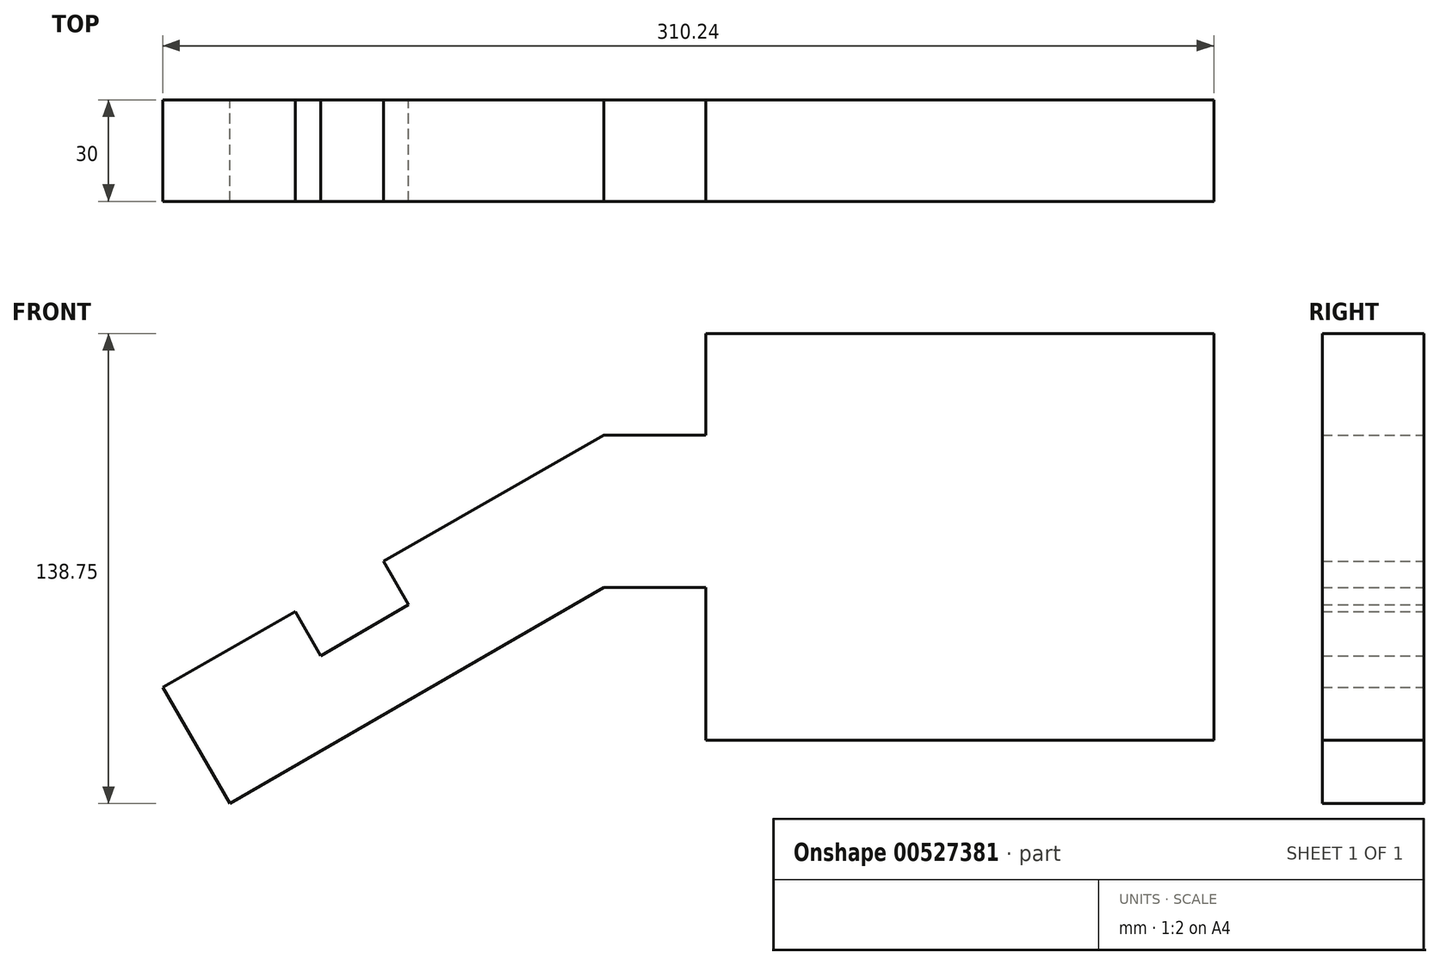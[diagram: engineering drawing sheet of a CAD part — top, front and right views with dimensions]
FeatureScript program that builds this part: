
annotation { "Feature Type Name" : "Feature", "Feature Type Description" : "" }
export const myFeature = defineFeature(function(context is Context, id is Id, definition is map)
    precondition{}
    {
        {
            var Q0;
            Q0=qCreatedBy(makeId("Front.planeOp"),FACE);
            var sketch = newSketch(context, id + "F0", { "sketchPlane" : qUnion([Q0])});
            skLineSegment(sketch, "E0", {"start": v(0, 0) * mm, "end": v(150, 0) * mm});
            skLineSegment(sketch, "E1", {"start": v(150, 0) * mm, "end": v(150, 120) * mm});
            skLineSegment(sketch, "E2", {"start": v(150, 120) * mm, "end": v(0, 120) * mm});
            skLineSegment(sketch, "E3", {"start": v(0, 0) * mm, "end": v(0, 45) * mm});
            skLineSegment(sketch, "E4", {"start": v(0, 120) * mm, "end": v(0, 90) * mm});
            skLineSegment(sketch, "E5", {"start": v(0, 90) * mm, "end": v(-30, 90) * mm});
            skLineSegment(sketch, "E6", {"start": v(0, 45) * mm, "end": v(-30, 45) * mm});
            skLineSegment(sketch, "E7", {"start": v(0, 90) * mm, "end": v(90, 90) * mm});
            skLineSegment(sketch, "E8", {"start": v(0, 45) * mm, "end": v(90, 45) * mm});
            skLineSegment(sketch, "E9", {"start": v(90, 45) * mm, "end": v(90, 90) * mm});
            skLineSegment(sketch, "E10", {"start": v(-30, 45) * mm, "end": v(-140.42, -18.75) * mm});
            skLineSegment(sketch, "E11", {"start": v(-140.42, -18.75) * mm, "end": v(-160.24, 15.58) * mm});
            skLineSegment(sketch, "E12", {"start": v(-30, 90) * mm, "end": v(-95.12, 52.8) * mm});
            skLineSegment(sketch, "E13", {"start": v(-121.1, 37.95) * mm, "end": v(-113.66, 24.92) * mm});
            skLineSegment(sketch, "E14", {"start": v(-113.66, 24.92) * mm, "end": v(-87.68, 39.92) * mm});
            skLineSegment(sketch, "E15", {"start": v(-87.68, 39.92) * mm, "end": v(-95.12, 52.95) * mm});
            skPoint(sketch, "E15.endSnap0", {"position": v(-95.12, 52.8) * mm});
            skLineSegment(sketch, "E16.trimOffspring", {"start": v(-121.1, 37.95) * mm, "end": v(-160.24, 15.58) * mm});
            skSolve(sketch);
        }
        {
            var Q0;
            Q0 = qSketchRegion(id + "F0", true);
            extrude(context, id + "F1", {"entities" : qUnion([Q0]), "depth" : 30 * mm, "offsetDistance" : 25 * mm});
        }
    });
